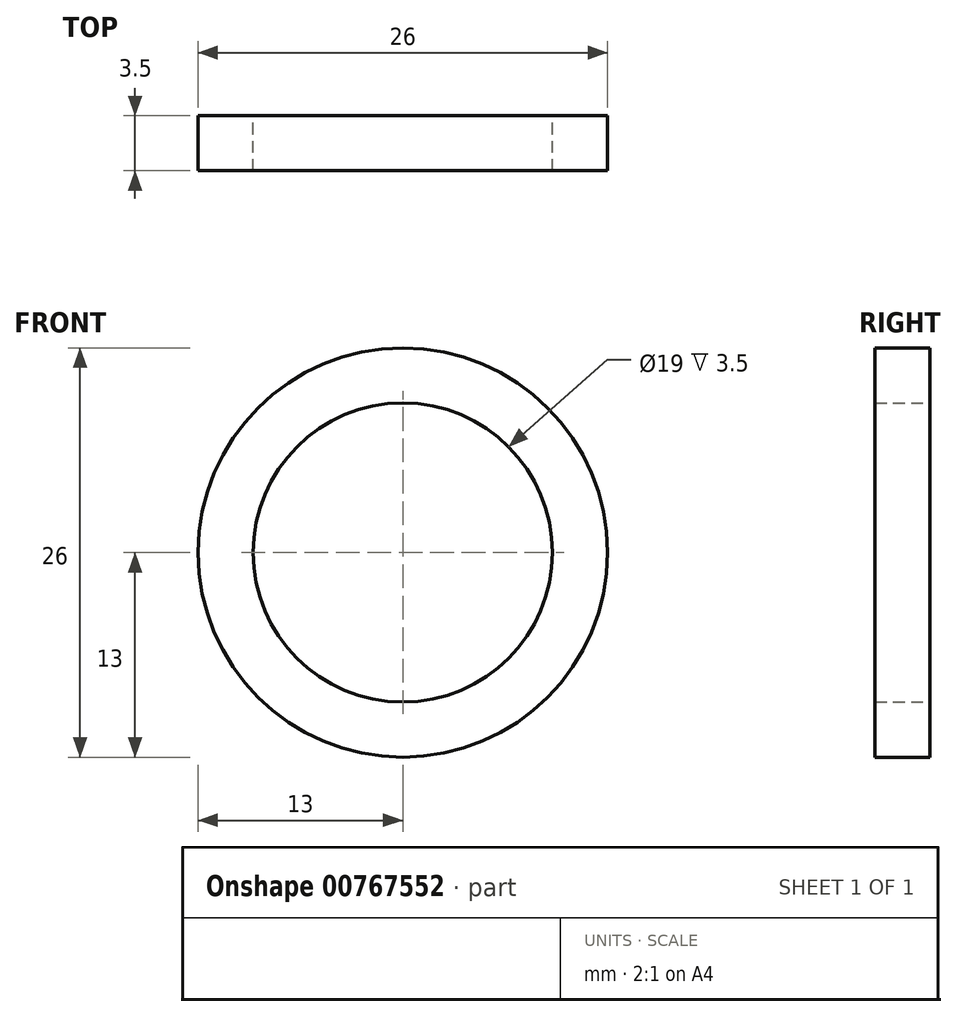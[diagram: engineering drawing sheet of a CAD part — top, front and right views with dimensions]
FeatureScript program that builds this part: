
annotation { "Feature Type Name" : "Feature", "Feature Type Description" : "" }
export const myFeature = defineFeature(function(context is Context, id is Id, definition is map)
    precondition{}
    {
        {
            var Q0;
            Q0=qCreatedBy(makeId("Front.planeOp"),FACE);
            var sketch = newSketch(context, id + "F0", { "sketchPlane" : qUnion([Q0])});
            skCircle(sketch, "E0", {"center": v(0, 0) * mm, "radius": 13 * mm});
            skCircle(sketch, "E1", {"center": v(0, 0) * mm, "radius": 9.5 * mm});
            skSolve(sketch);
        }
        {
            var Q0;
            Q0=makeQuery(id+"F0.imprint","IMPRINT",FACE,{"disambiguationData":[TD([[makeQuery(id+"F0.imprint","IMPRINT",EDGE,{"derivedFrom":sQuery(id+"F0.wireOp",EDGE,"E0")}),1.0]])]});
            extrude(context, id + "F1", {"entities" : qUnion([Q0]), "depth" : 3.5 * mm, "offsetDistance" : 25 * mm});
        }
    });
